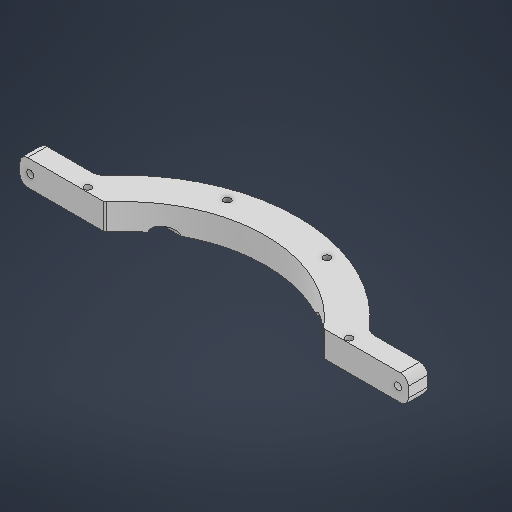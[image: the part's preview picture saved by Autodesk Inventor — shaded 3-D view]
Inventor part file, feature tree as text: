
AUTODESK INVENTOR PART (.ipt)
format: ipt  version: 2025 (Build 290162000, 162)  size: 324,608 bytes
history: native  units: in
note: dims shown in document units (in); Inventor stores cm internally (conversion verified against a paired STEP export)
features: sketch x7, extrude x4, fillet x4, hole x2, mirror x2, projected_geometry x1
ambient origin geometry x8: Origin, YZ Plane, XZ Plane, XY Plane, X Axis, Y Axis, Z Axis, Center Point
bodies: Solid1 (feature_tree)
feature tree (20):
  extrude  "Extrusion1"  Depth=8.6614in
  extrude  "Extrusion3"  Depth=3.9469in
  fillet  "Fillet1"  Radius=0.9843in
  fillet  "Fillet2"  Radius=0.5906in
  fillet  "Fillet3"  Radius=0.7874in
  hole  "Hole2"  [1 undecoded]
  mirror  "Mirror1"
  mirror  "Mirror2"
  hole  "Hole3"  [1 undecoded]
  extrude  "Extrusion7"  Depth=0.3937in
  fillet  "Fillet7"  Radius=0.3937in
  extrude  "Extrusion11"  Depth=0.3937in
  sketch  "Sketch1"  dims[d0=10.6299in d1=8.6614in]
  sketch  "Sketch4"  dims[d25=0.5906in d26=0.0in d27=0.0in]
  projected_geometry  "Projected Loop1"
  sketch  "Sketch5"  dims[d28=0.2362in d29=0.3937in]
  sketch  "Sketch7"  dims[d30=0.0787in]
  sketch  "Sketch11"  dims[d31=0.2165in d32=0.2362in d33=0.3465in d34=0.1969in d35=90.0deg d36=0.315in d37=0.8108in d38=0.315in d39=0.3937in]
  sketch  "Sketch Circular Pattern3"  dims[d2=0.7874in d3=0.0in d21=3.9469in d22=0.9843in d23=0.5906in d24=0.7874in]
  sketch  "Sketch15"  dims[d43=0.1969in d44=0.2362in d45=0.1575in d46=0.0787in d47=90.0deg d48=0.315in d49=0.8108in d50=5.0197in d57=0.3937in d61=0.0in d62=0.0in d63=0.0787in d69=9.8425in d75=0.2165in d76=3.937in d78=360.0deg d85=0.0in d86=0.0in d87=0.3937in d88=0.7874in]
note: 2 required parameter values undecoded (feature->parameter linkage not recoverable at this tier; creation-order binding heuristic only, values carry confidence <= 0.55)
